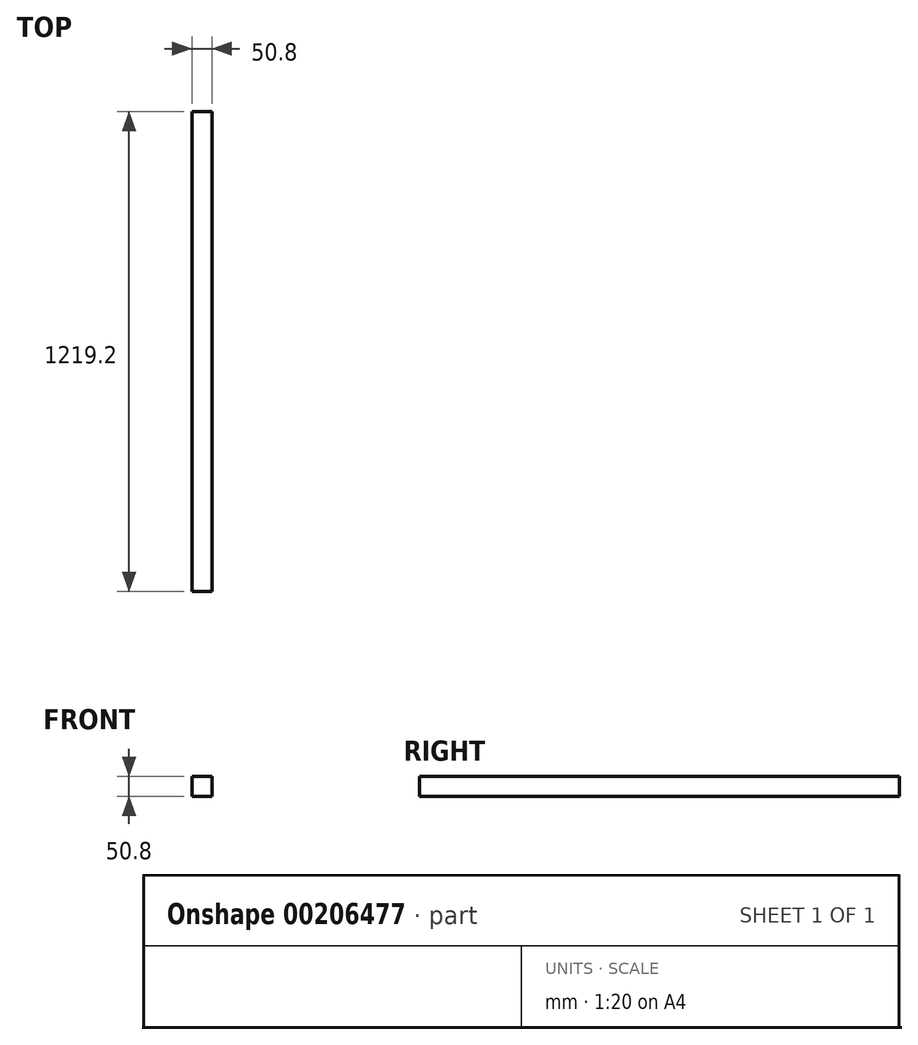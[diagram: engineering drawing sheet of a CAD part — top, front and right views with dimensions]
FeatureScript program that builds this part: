
annotation { "Feature Type Name" : "Feature", "Feature Type Description" : "" }
export const myFeature = defineFeature(function(context is Context, id is Id, definition is map)
    precondition{}
    {
        {
            var Q0;
            Q0=qCreatedBy(makeId("Front.planeOp"),FACE);
            var sketch = newSketch(context, id + "F0", { "sketchPlane" : qUnion([Q0])});
            skLineSegment(sketch, "E0.bottom", {"start": v(25.4, -25.4) * mm, "end": v(-25.4, -25.4) * mm});
            skLineSegment(sketch, "E0.top", {"start": v(25.4, 25.4) * mm, "end": v(-25.4, 25.4) * mm});
            skLineSegment(sketch, "E0.left", {"start": v(25.4, -25.4) * mm, "end": v(25.4, 25.4) * mm});
            skLineSegment(sketch, "E0.right", {"start": v(-25.4, -25.4) * mm, "end": v(-25.4, 25.4) * mm});
            skPoint(sketch, "E0.middle", {"position": v(0, 0) * mm});
            skSolve(sketch);
        }
        {
            var Q0;
            Q0 = qSketchRegion(id + "F0", true);
            extrude(context, id + "F1", {"entities" : qUnion([Q0]), "depth" : 1219.2 * mm});
        }
    });
